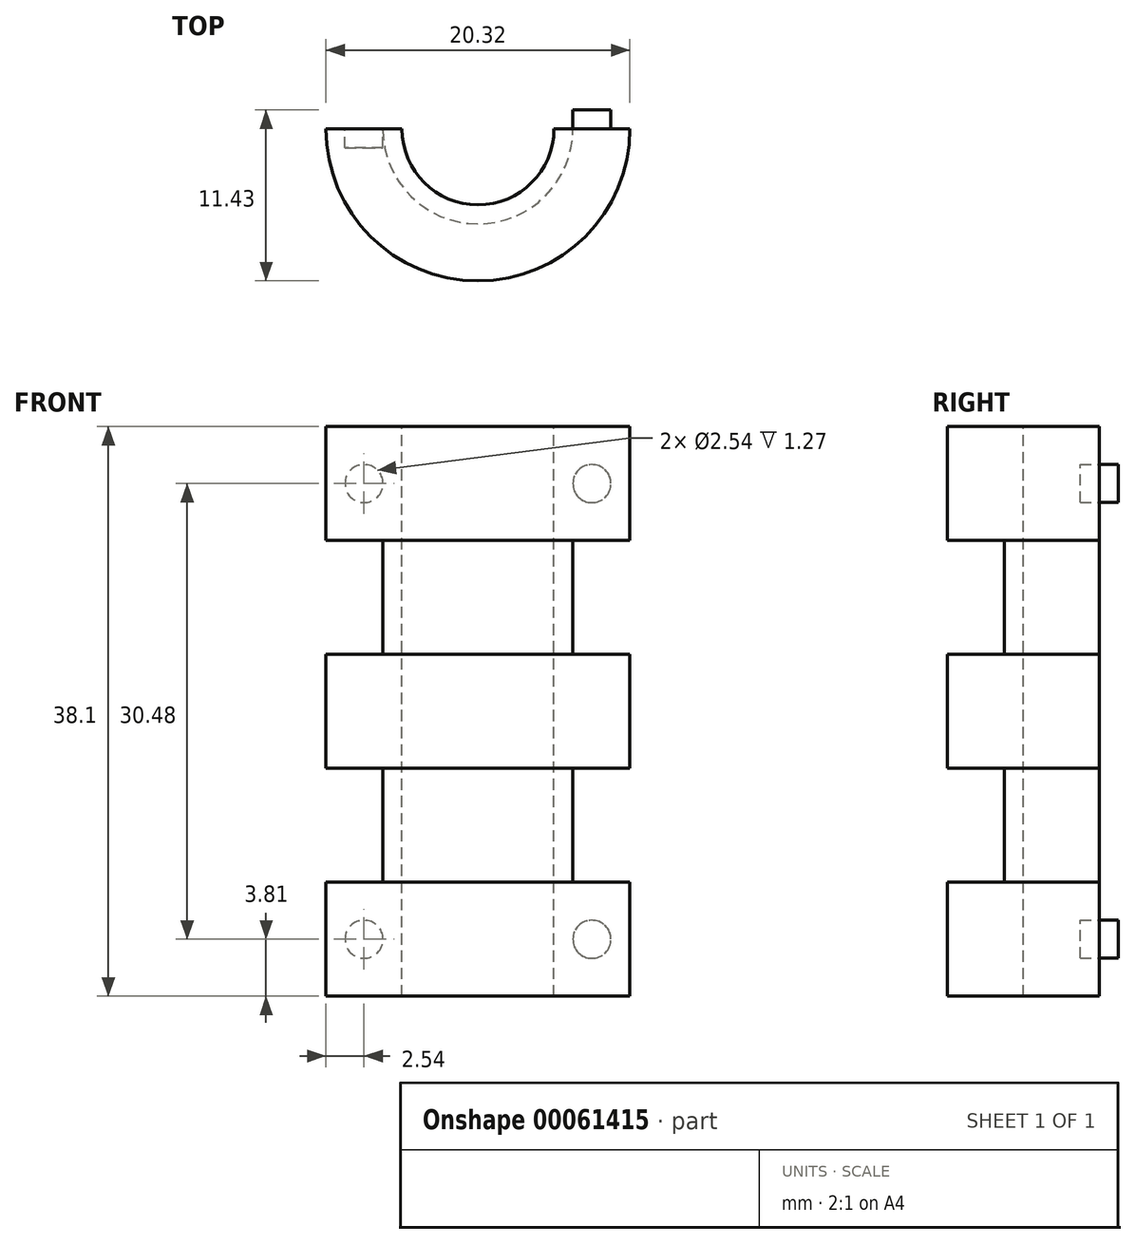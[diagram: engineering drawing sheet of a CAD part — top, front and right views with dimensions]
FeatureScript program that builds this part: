
annotation { "Feature Type Name" : "Feature", "Feature Type Description" : "" }
export const myFeature = defineFeature(function(context is Context, id is Id, definition is map)
    precondition{}
    {
        {
            var Q0;
            Q0=qCreatedBy(makeId("Front.planeOp"),FACE);
            var sketch = newSketch(context, id + "F0", { "sketchPlane" : qUnion([Q0])});
            skLineSegment(sketch, "E0", {"start": v(0, 19.05) * mm, "end": v(-10.16, 19.05) * mm});
            skLineSegment(sketch, "E1", {"start": v(-10.16, 19.05) * mm, "end": v(-10.16, 11.43) * mm});
            skLineSegment(sketch, "E2", {"start": v(-10.16, 11.43) * mm, "end": v(-6.35, 11.43) * mm});
            skLineSegment(sketch, "E3", {"start": v(-6.35, 11.43) * mm, "end": v(-6.35, 3.81) * mm});
            skLineSegment(sketch, "E4", {"start": v(-6.35, 3.81) * mm, "end": v(-10.16, 3.81) * mm});
            skLineSegment(sketch, "E5", {"start": v(-10.16, 3.8) * mm, "end": v(-10.16, -3.81) * mm});
            skLineSegment(sketch, "E6", {"start": v(-10.16, -3.81) * mm, "end": v(-6.35, -3.81) * mm});
            skLineSegment(sketch, "E7", {"start": v(-6.35, -3.81) * mm, "end": v(-6.35, -11.43) * mm});
            skLineSegment(sketch, "E8", {"start": v(-6.35, -11.43) * mm, "end": v(-10.16, -11.43) * mm});
            skLineSegment(sketch, "E9", {"start": v(-10.16, -11.43) * mm, "end": v(-10.16, -19.05) * mm});
            skLineSegment(sketch, "E10", {"start": v(-10.16, -19.05) * mm, "end": v(0, -19.05) * mm});
            skLineSegment(sketch, "E11", {"start": v(0, -19.05) * mm, "end": v(0, 19.05) * mm});
            skSolve(sketch);
        }
        {
            var Q0;
            Q0=makeQuery(id+"F0.imprint","IMPRINT",FACE,{"disambiguationData":[TD([[makeQuery(id+"F0.imprint","IMPRINT",EDGE,{"derivedFrom":sQuery(id+"F0.wireOp",EDGE,"E0")}),1.0]])]});
            var Q1;
            Q1=sQuery(id+"F0.wireOp",EDGE,"E11");
            revolve(context, id + "F1", {"entities" : qUnion([Q0]), "axis" : qUnion([Q1]), "revolveType" : RevolveType.ONE_DIRECTION, "angle" : 180 * degree});
        }
        {
            var Q0;
            Q0=qCreatedBy(makeId("Top.planeOp"),FACE);
            var sketch = newSketch(context, id + "F2", { "sketchPlane" : qUnion([Q0])});
            skArc(sketch, "E12", {"start": v(5.08, 0) * mm, "mid": v(0, -5.08) * mm, "end": v(-5.08, 0) * mm});
            skLineSegment(sketch, "E13", {"start": v(5.08, 0) * mm, "end": v(-5.08, 0) * mm});
            skSolve(sketch);
        }
        {
            var Q0;
            Q0 = qSketchRegion(id + "F2", true);
            extrude(context, id + "F3", {"entities" : qUnion([Q0]), "operationType" : NewBodyOperationType.REMOVE, "endBound" : BoundingType.SYMMETRIC, "oppositeDirection" : true, "depth" : 50.8 * mm});
        }
        {
            var Q0;
            Q0=qCreatedBy(makeId("Front.planeOp"),FACE);
            var sketch = newSketch(context, id + "F4", { "sketchPlane" : qUnion([Q0])});
            skCircle(sketch, "E14", {"center": v(7.62, 15.24) * mm, "radius": 1.27 * mm});
            skCircle(sketch, "E15", {"center": v(7.62, -15.24) * mm, "radius": 1.27 * mm});
            skSolve(sketch);
        }
        {
            var Q0;
            Q0 = qSketchRegion(id + "F4", true);
            extrude(context, id + "F5", {"entities" : qUnion([Q0]), "operationType" : NewBodyOperationType.ADD, "oppositeDirection" : true, "depth" : 1.27 * mm});
        }
        {
            var Q0;
            Q0=qCreatedBy(makeId("Front.planeOp"),FACE);
            var sketch = newSketch(context, id + "F6", { "sketchPlane" : qUnion([Q0])});
            skCircle(sketch, "E16", {"center": v(-7.62, 15.24) * mm, "radius": 1.27 * mm});
            skCircle(sketch, "E17", {"center": v(-7.62, -15.24) * mm, "radius": 1.27 * mm});
            skSolve(sketch);
        }
        {
            var Q0;
            Q0 = qSketchRegion(id + "F6", true);
            extrude(context, id + "F7", {"entities" : qUnion([Q0]), "operationType" : NewBodyOperationType.REMOVE, "depth" : 1.27 * mm});
        }
    });
